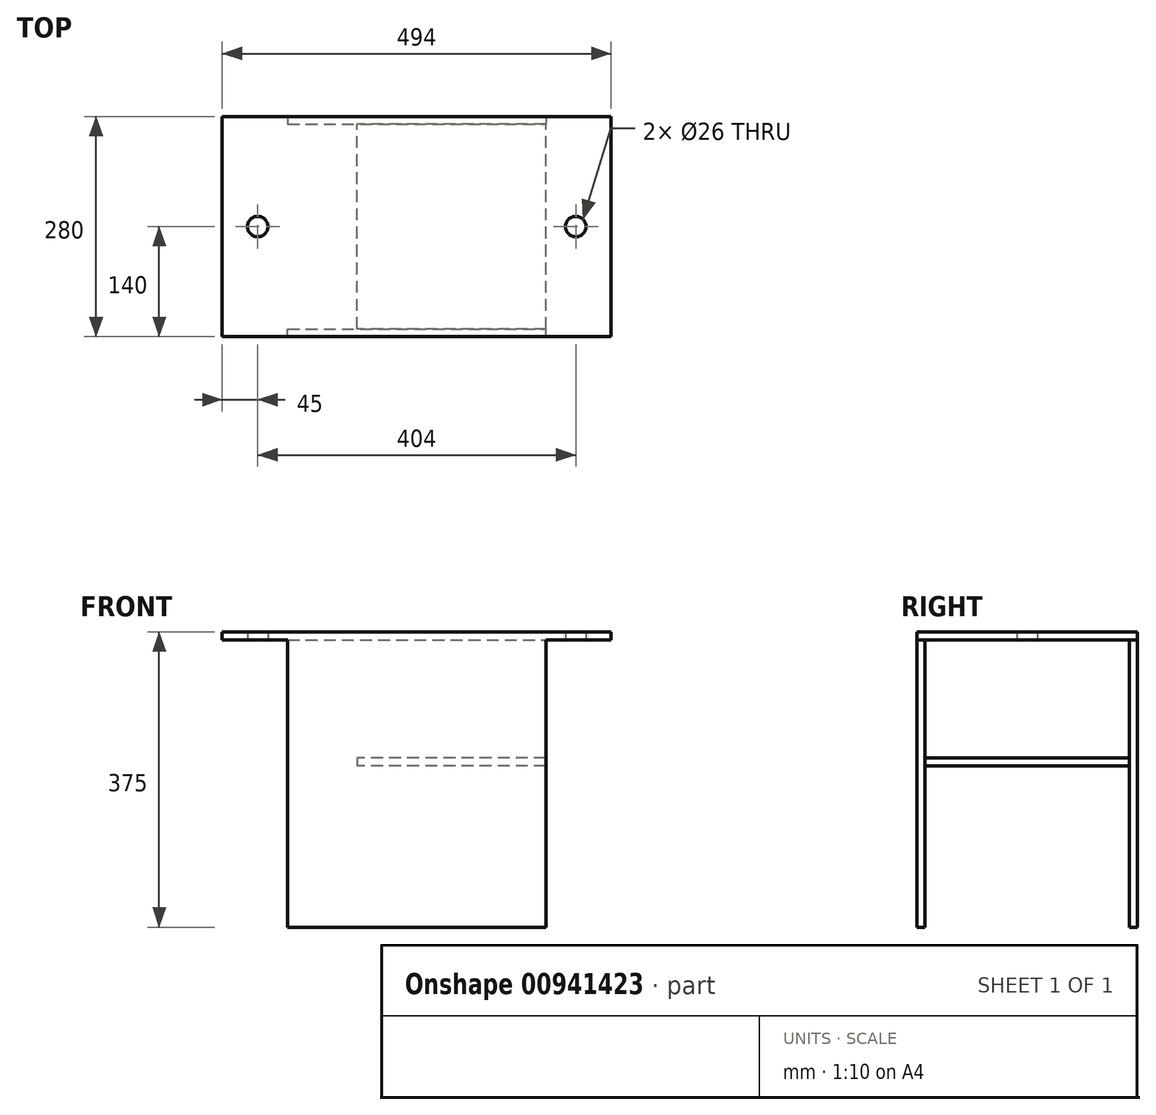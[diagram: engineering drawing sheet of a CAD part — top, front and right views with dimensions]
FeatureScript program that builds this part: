
annotation { "Feature Type Name" : "Feature", "Feature Type Description" : "" }
export const myFeature = defineFeature(function(context is Context, id is Id, definition is map)
    precondition{}
    {
        {
            var Q0;
            Q0=qCreatedBy(makeId("Top.planeOp"),FACE);
            var sketch = newSketch(context, id + "F0", { "sketchPlane" : qUnion([Q0])});
            skLineSegment(sketch, "E0.bottom", {"start": v(0, 0) * mm, "end": v(494, 0) * mm});
            skLineSegment(sketch, "E0.top", {"start": v(0, 280) * mm, "end": v(494, 280) * mm});
            skLineSegment(sketch, "E0.left", {"start": v(0, 0) * mm, "end": v(0, 280) * mm});
            skLineSegment(sketch, "E0.right", {"start": v(494, 0) * mm, "end": v(494, 280) * mm});
            skCircle(sketch, "E1", {"center": v(45, 140) * mm, "radius": 13 * mm});
            skCircle(sketch, "E2", {"center": v(449, 140) * mm, "radius": 13 * mm});
            skLineSegment(sketch, "E3", {"start": v(449, 140) * mm, "end": v(494, 140) * mm});
            skLineSegment(sketch, "E4", {"start": v(494, 140) * mm, "end": v(449, 140) * mm});
            skLineSegment(sketch, "E5", {"start": v(449, 0) * mm, "end": v(449, 140) * mm});
            skLineSegment(sketch, "E6", {"start": v(45, 140) * mm, "end": v(0, 140) * mm});
            skLineSegment(sketch, "E7", {"start": v(0, 140) * mm, "end": v(45, 140) * mm});
            skLineSegment(sketch, "E8", {"start": v(45, 0) * mm, "end": v(45, 140) * mm});
            skSolve(sketch);
        }
        {
            var Q0;
            Q0 = qSketchRegion(id + "F0", true);
            extrude(context, id + "F1", {"entities" : qUnion([Q0]), "depth" : 10 * mm, "offsetDistance" : 25 * mm});
        }
        {
            var Q0;
            Q0=makeQuery(id+"F1.opExtrude","CAP_FACE",FACE,{"disambiguationData":[OSD([sQuery(id+"F0.wireOp",EDGE,"E0.bottom"),sQuery(id+"F0.wireOp",EDGE,"E0.top"),sQuery(id+"F0.wireOp",EDGE,"E0.left"),sQuery(id+"F0.wireOp",EDGE,"E0.right"),sQuery(id+"F0.wireOp",EDGE,"E1"),sQuery(id+"F0.wireOp",EDGE,"E2")])],"isStart":true});
            var sketch = newSketch(context, id + "F2", { "sketchPlane" : qUnion([Q0])});
            skLineSegment(sketch, "E9.bottom", {"start": v(83, -280) * mm, "end": v(411, -280) * mm});
            skLineSegment(sketch, "E9.top", {"start": v(83, -270) * mm, "end": v(411, -270) * mm});
            skLineSegment(sketch, "E9.left", {"start": v(83, -280) * mm, "end": v(83, -270) * mm});
            skLineSegment(sketch, "E9.right", {"start": v(411, -280) * mm, "end": v(411, -270) * mm});
            skLineSegment(sketch, "E10", {"start": v(83, -270) * mm, "end": v(0, -270) * mm});
            skLineSegment(sketch, "E11.bottom", {"start": v(83, 0) * mm, "end": v(411, 0) * mm});
            skLineSegment(sketch, "E11.top", {"start": v(83, -10) * mm, "end": v(411, -10) * mm});
            skLineSegment(sketch, "E11.left", {"start": v(83, 0) * mm, "end": v(83, -10) * mm});
            skLineSegment(sketch, "E11.right", {"start": v(411, 0) * mm, "end": v(411, -10) * mm});
            skLineSegment(sketch, "E12", {"start": v(83, -10) * mm, "end": v(0, -10) * mm});
            skSolve(sketch);
        }
        {
            var Q0;
            Q0 = qSketchRegion(id + "F2", true);
            extrude(context, id + "F3", {"entities" : qUnion([Q0]), "operationType" : NewBodyOperationType.ADD, "depth" : 365 * mm, "offsetDistance" : 25 * mm});
        }
        {
            var Q0;
            Q0=makeQuery(id+"F3.opExtrude","SWEPT_FACE",FACE,{"disambiguationData":[OSD([sQuery(id+"F2.wireOp",EDGE,"E9.top")])]});
            var sketch = newSketch(context, id + "F4", { "sketchPlane" : qUnion([Q0])});
            skLineSegment(sketch, "E13.bottom", {"start": v(411, -150) * mm, "end": v(171, -150) * mm});
            skLineSegment(sketch, "E13.top", {"start": v(411, -160) * mm, "end": v(171, -160) * mm});
            skLineSegment(sketch, "E13.left", {"start": v(411, -150) * mm, "end": v(411, -160) * mm});
            skLineSegment(sketch, "E13.right", {"start": v(171, -150) * mm, "end": v(171, -160) * mm});
            skLineSegment(sketch, "E14", {"start": v(411, -150) * mm, "end": v(411, 0) * mm});
            skSolve(sketch);
        }
        {
            var Q0;
            Q0 = qSketchRegion(id + "F4", true);
            extrude(context, id + "F5", {"entities" : qUnion([Q0]), "depth" : 260 * mm, "offsetDistance" : 25 * mm});
        }
    });
